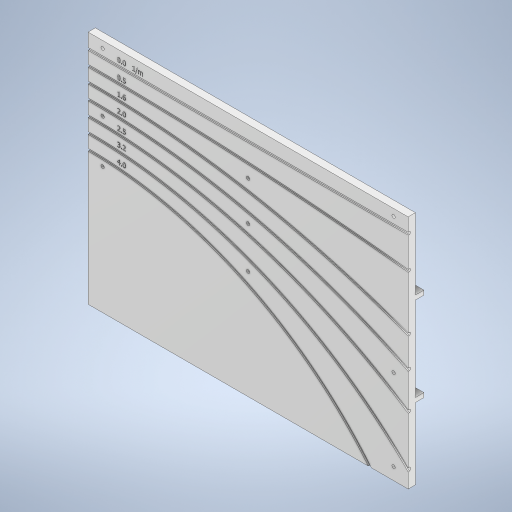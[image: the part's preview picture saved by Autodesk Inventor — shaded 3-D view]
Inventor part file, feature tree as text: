
AUTODESK INVENTOR PART (.ipt)
format: ipt  version: 2023 (Build 270158000, 158)  size: 1,054,208 bytes
history: native  units: mm
features: sketch x17, sweep x7, extrude x3, other x1
ambient origin geometry x8: Origin, YZ Plane, XZ Plane, XY Plane, X Axis, Y Axis, Z Axis, Center Point
bodies: Solide1 (feature_tree)
feature tree (28):
  extrude  "Extrusion1"  Depth=220.0mm
  extrude  "Extrusion2"  Depth=162.0mm
  sweep  "Balayage1"
  sweep  "Balayage2"
  sweep  "Balayage3"
  sweep  "Balayage4"
  sweep  "Balayage5"
  sweep  "Balayage6"
  sweep  "Balayage7"
  other  "Gravure1"
  extrude  "Extrusion3"  TaperAngle=0.0deg  [1 undecoded]
  sketch  "Esquisse1"
  sketch  "Esquisse3"
  sketch  "Esquisse4"
  sketch  "Esquisse5"
  sketch  "Esquisse6"
  sketch  "Esquisse7"
  sketch  "Esquisse8"
  sketch  "Esquisse9"
  sketch  "Esquisse10"
  sketch  "Esquisse11"
  sketch  "Esquisse12"
  sketch  "Esquisse13"
  sketch  "Esquisse14"
  sketch  "Esquisse15"
  sketch  "Esquisse16"
  sketch  "Esquisse18"
  sketch  "Esquisse19"
note: 1 required parameter value undecoded (feature->parameter linkage not recoverable at this tier; creation-order binding heuristic only, values carry confidence <= 0.55)
